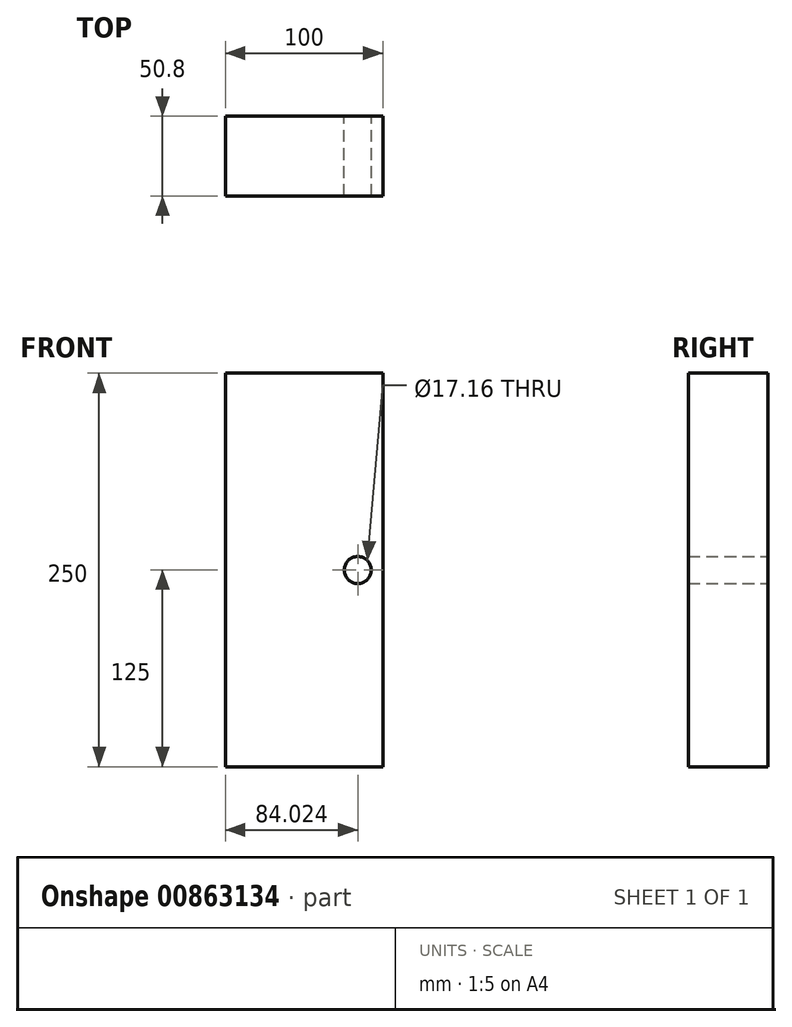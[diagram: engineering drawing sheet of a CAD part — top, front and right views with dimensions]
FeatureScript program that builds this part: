
annotation { "Feature Type Name" : "Feature", "Feature Type Description" : "" }
export const myFeature = defineFeature(function(context is Context, id is Id, definition is map)
    precondition{}
    {
        {
            var Q0;
            Q0=qCreatedBy(makeId("Front.planeOp"),FACE);
            var sketch = newSketch(context, id + "F0", { "sketchPlane" : qUnion([Q0])});
            skLineSegment(sketch, "E0.bottom", {"start": v(-50, 125) * mm, "end": v(50, 125) * mm});
            skLineSegment(sketch, "E0.top", {"start": v(-50, -125) * mm, "end": v(50, -125) * mm});
            skLineSegment(sketch, "E0.left", {"start": v(-50, 125) * mm, "end": v(-50, -125) * mm});
            skLineSegment(sketch, "E0.right", {"start": v(50, 125) * mm, "end": v(50, -125) * mm});
            skPoint(sketch, "E0.middle", {"position": v(0, 0) * mm});
            skCircle(sketch, "E1", {"center": v(34.02, 0) * mm, "radius": 8.58 * mm});
            skLineSegment(sketch, "E2", {"start": v(50, -125) * mm, "end": v(70, -125.2) * mm});
            skLineSegment(sketch, "E3.0", {"start": v(52.58, 124.99) * mm, "end": v(72.58, 124.78) * mm});
            skLineSegment(sketch, "E4", {"start": v(72.58, 124.78) * mm, "end": v(70, -125.2) * mm});
            skSolve(sketch);
        }
        {
            var Q0;
            Q0=makeQuery(id+"F0.imprint","IMPRINT",FACE,{"disambiguationData":[TD([[makeQuery(id+"F0.imprint","IMPRINT",EDGE,{"derivedFrom":sQuery(id+"F0.wireOp",EDGE,"E0.bottom")}),-1.0]])]});
            extrude(context, id + "F1", {"entities" : qUnion([Q0]), "endBound" : BoundingType.SYMMETRIC, "depth" : 50.8 * mm, "offsetDistance" : 25.4 * mm});
        }
    });
